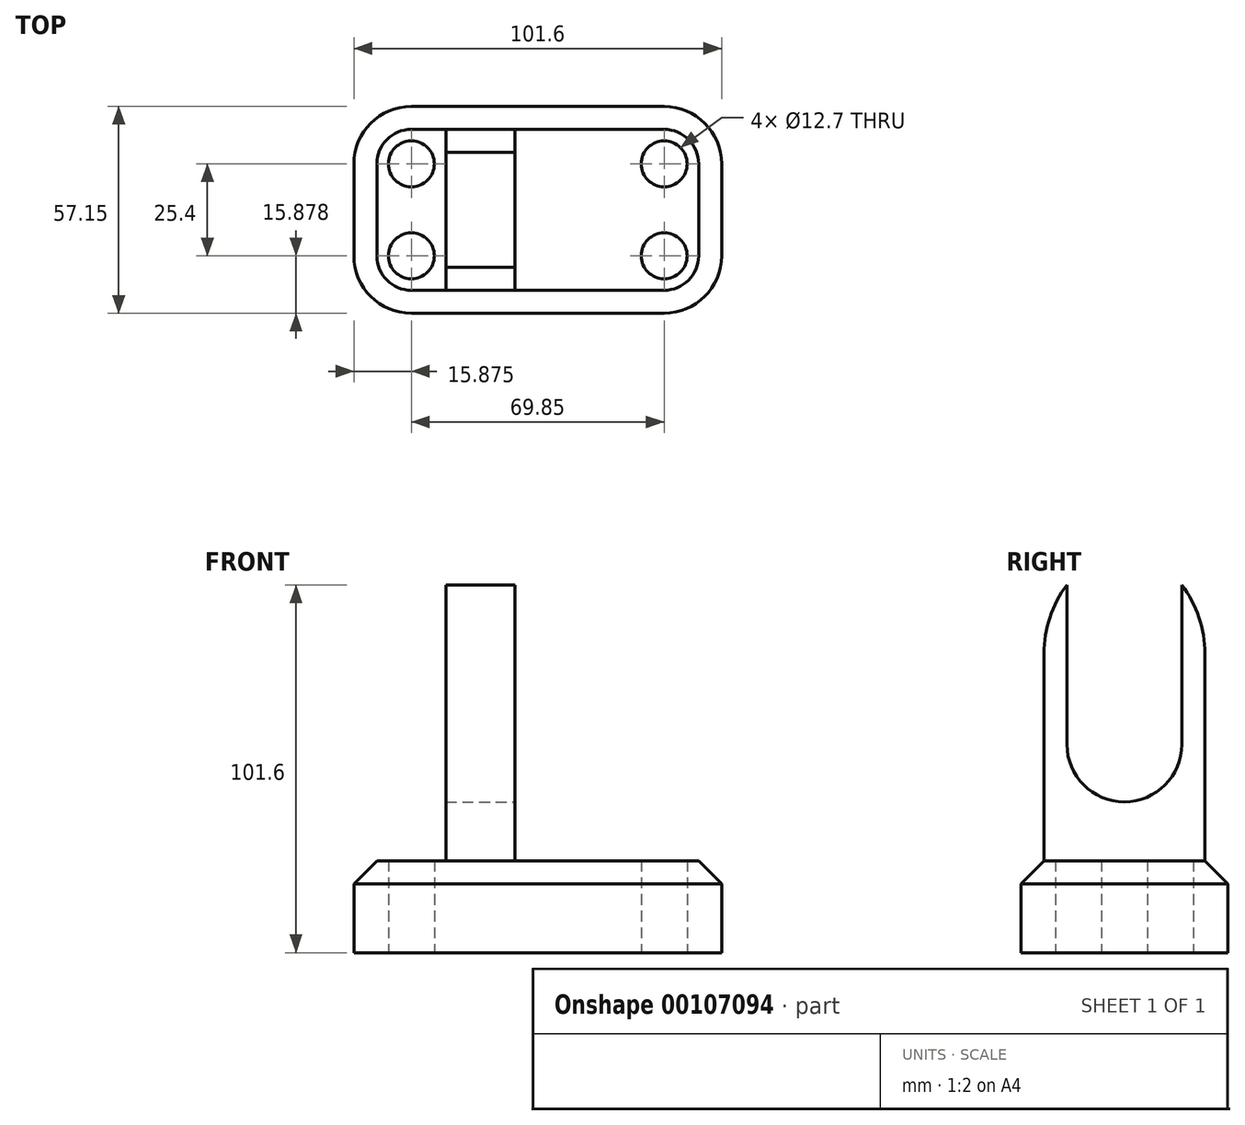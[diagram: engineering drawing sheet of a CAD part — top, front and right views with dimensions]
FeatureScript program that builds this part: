
annotation { "Feature Type Name" : "Feature", "Feature Type Description" : "" }
export const myFeature = defineFeature(function(context is Context, id is Id, definition is map)
    precondition{}
    {
        {
            var Q0;
            Q0=qCreatedBy(makeId("Top.planeOp"),FACE);
            var sketch = newSketch(context, id + "F0", { "sketchPlane" : qUnion([Q0])});
            skLineSegment(sketch, "E0.bottom", {"start": v(-74.82, 42.82) * mm, "end": v(-4.97, 42.82) * mm});
            skLineSegment(sketch, "E0.top", {"start": v(-74.82, -14.33) * mm, "end": v(-4.97, -14.33) * mm});
            skLineSegment(sketch, "E0.left", {"start": v(-90.7, 26.95) * mm, "end": v(-90.7, 1.55) * mm});
            skLineSegment(sketch, "E0.right", {"start": v(10.9, 26.95) * mm, "end": v(10.9, 1.55) * mm});
            skPoint(sketch, "E1.visualSharp", {"position": v(10.9, 42.82) * mm});
            skArc(sketch, "E1.filletArc", {"start": v(10.9, 26.95) * mm, "mid": v(6.25, 38.17) * mm, "end": v(-4.97, 42.82) * mm});
            skPoint(sketch, "E2.visualSharp", {"position": v(10.9, -14.33) * mm});
            skArc(sketch, "E2.filletArc", {"start": v(-4.97, -14.33) * mm, "mid": v(6.25, -9.68) * mm, "end": v(10.9, 1.55) * mm});
            skPoint(sketch, "E3.visualSharp", {"position": v(-90.7, -14.33) * mm});
            skArc(sketch, "E3.filletArc", {"start": v(-90.7, 1.55) * mm, "mid": v(-86.05, -9.68) * mm, "end": v(-74.82, -14.33) * mm});
            skPoint(sketch, "E4.visualSharp", {"position": v(-90.7, 42.82) * mm});
            skArc(sketch, "E4.filletArc", {"start": v(-74.82, 42.82) * mm, "mid": v(-86.05, 38.17) * mm, "end": v(-90.7, 26.95) * mm});
            skCircle(sketch, "E5", {"center": v(-74.82, 26.95) * mm, "radius": 6.35 * mm});
            skCircle(sketch, "E6", {"center": v(-4.97, 26.95) * mm, "radius": 6.35 * mm});
            skCircle(sketch, "E7", {"center": v(-4.97, 1.55) * mm, "radius": 6.35 * mm});
            skCircle(sketch, "E8", {"center": v(-74.82, 1.55) * mm, "radius": 6.35 * mm});
            skSolve(sketch);
        }
        {
            var Q0;
            Q0=makeQuery(id+"F0.imprint","IMPRINT",FACE,{"disambiguationData":[TD([[makeQuery(id+"F0.imprint","IMPRINT",EDGE,{"derivedFrom":sQuery(id+"F0.wireOp",EDGE,"E0.bottom")}),-1.0]])]});
            extrude(context, id + "F1", {"entities" : qUnion([Q0]), "depth" : 25.4 * mm});
        }
        {
            var Q0;
            Q0=makeQuery(id+"F1.opExtrude","CAP_EDGE",EDGE,{"disambiguationData":[OSD([sQuery(id+"F0.wireOp",EDGE,"E2.filletArc")])],"isStart":false});
            chamfer(context, id + "F2", {"entities" : qUnion([Q0]), "width" : 6.35 * mm, "tangentPropagation" : true});
        }
        {
            var Q0;
            Q0=makeQuery(id+"F1.opExtrude","CAP_FACE",FACE,{"disambiguationData":[OSD([sQuery(id+"F0.wireOp",EDGE,"E0.bottom"),sQuery(id+"F0.wireOp",EDGE,"E0.top"),sQuery(id+"F0.wireOp",EDGE,"E0.left"),sQuery(id+"F0.wireOp",EDGE,"E0.right"),sQuery(id+"F0.wireOp",EDGE,"E1.filletArc"),sQuery(id+"F0.wireOp",EDGE,"E2.filletArc"),sQuery(id+"F0.wireOp",EDGE,"E3.filletArc"),sQuery(id+"F0.wireOp",EDGE,"E4.filletArc"),sQuery(id+"F0.wireOp",EDGE,"E5"),sQuery(id+"F0.wireOp",EDGE,"E6"),sQuery(id+"F0.wireOp",EDGE,"E7"),sQuery(id+"F0.wireOp",EDGE,"E8")])],"isStart":false});
            var sketch = newSketch(context, id + "F3", { "sketchPlane" : qUnion([Q0])});
            skLineSegment(sketch, "E9.bottom", {"start": v(-46.25, -7.98) * mm, "end": v(-65.3, -7.98) * mm});
            skLineSegment(sketch, "E9.top", {"start": v(-46.25, 36.47) * mm, "end": v(-65.3, 36.47) * mm});
            skLineSegment(sketch, "E9.left", {"start": v(-46.25, -7.98) * mm, "end": v(-46.25, 36.47) * mm});
            skLineSegment(sketch, "E9.right", {"start": v(-65.3, -7.98) * mm, "end": v(-65.3, 36.47) * mm});
            skPoint(sketch, "E10.end.orphan", {"position": v(-46.25, 14.25) * mm});
            skPoint(sketch, "E10.start.orphan", {"position": v(4.55, 14.25) * mm});
            skSolve(sketch);
        }
        {
            var Q0;
            Q0 = qSketchRegion(id + "F3", true);
            extrude(context, id + "F4", {"entities" : qUnion([Q0]), "operationType" : NewBodyOperationType.ADD, "depth" : 76.2 * mm});
        }
        {
            var Q0;
            Q0=makeQuery(id+"F4.opExtrude","SWEPT_FACE",FACE,{"disambiguationData":[OSD([sQuery(id+"F3.wireOp",EDGE,"E9.left")])]});
            var sketch = newSketch(context, id + "F5", { "sketchPlane" : qUnion([Q0])});
            skLineSegment(sketch, "E11", {"start": v(14.25, 19.44) * mm, "end": v(14.25, 57.54) * mm});
            skPoint(sketch, "E11.startSnap0", {"position": v(14.25, 25.4) * mm});
            skCircle(sketch, "E12", {"center": v(14.25, 57.54) * mm, "radius": 15.88 * mm});
            skSolve(sketch);
        }
        {
            var Q0;
            Q0 = qSketchRegion(id + "F5", true);
            extrude(context, id + "F6", {"entities" : qUnion([Q0]), "operationType" : NewBodyOperationType.REMOVE, "endBound" : BoundingType.UP_TO_NEXT, "oppositeDirection" : true, "depth" : 25.4 * mm});
        }
        {
            var Q0;
            Q0=makeQuery(id+"F4.opExtrude","SWEPT_FACE",FACE,{"disambiguationData":[OSD([sQuery(id+"F3.wireOp",EDGE,"E9.left")])]});
            var sketch = newSketch(context, id + "F7", { "sketchPlane" : qUnion([Q0])});
            skLineSegment(sketch, "E13", {"start": v(14.25, 57.54) * mm, "end": v(30.12, 57.54) * mm});
            skLineSegment(sketch, "E14", {"start": v(14.25, 57.54) * mm, "end": v(-1.63, 57.54) * mm});
            skLineSegment(sketch, "E15", {"start": v(-1.63, 57.54) * mm, "end": v(-1.63, 101.6) * mm});
            skLineSegment(sketch, "E16", {"start": v(30.12, 57.54) * mm, "end": v(30.12, 101.6) * mm});
            skSolve(sketch);
        }
        {
            var Q0;
            {var subQ0=sQuery(id+"F7.wireOp",EDGE,"E15");Q0=makeQuery(id+"F7.imprint","IMPRINT",FACE,{"disambiguationData":[TD([[makeQuery(id+"F7.imprint","IMPRINT",EDGE,{"derivedFrom":subQ0}),-1.0]])]});}
            extrude(context, id + "F8", {"entities" : qUnion([Q0]), "operationType" : NewBodyOperationType.REMOVE, "oppositeDirection" : true, "depth" : 25.4 * mm});
        }
        {
            var Q0;
            Q0=makeQuery(id+"F4.opExtrude","CAP_EDGE",EDGE,{"disambiguationData":[OSD([sQuery(id+"F3.wireOp",EDGE,"E9.bottom")])],"isStart":false});
            var Q1;
            Q1=makeQuery(id+"F4.opExtrude","CAP_EDGE",EDGE,{"disambiguationData":[OSD([sQuery(id+"F3.wireOp",EDGE,"E9.top")])],"isStart":false});
            fillet(context, id + "F9", {"entities" : qUnion([Q0, Q1]), "radius" : 31.75 * mm, "tangentPropagation" : true, "allowEdgeOverflow" : false});
        }
    });
